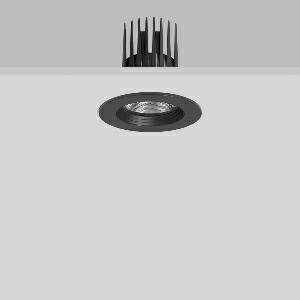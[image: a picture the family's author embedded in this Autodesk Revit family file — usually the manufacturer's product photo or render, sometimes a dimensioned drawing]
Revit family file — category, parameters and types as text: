
# Revit family: heledon_mini_e_901749_003_76_e557
name_source: partatom
category: Lighting Fixtures
units: mm (PartAtom-declared; Revit-internal decimal feet)

## family parameters
Cut with Voids When Loaded = No
Host = Face
Light Source = No
Part Type = Normal
Room Calculation Point = No
Round Connector Dimension = Use Diameter
Shared = No

## types (1)
- HELEDON mini E (1 x LED Modul 930, 3500 lm, 3000)
    Apparent Load = 29 VA
    Approval mark = CE
    CIE Flux Codes = 99 100 100 100 100
    Color Rendering = 90
    Color Temperature = 3000
    Default Elevation = 1800 mm
    Description = Series: HELEDON mini
Round recessed downlight. Housing: die-cast aluminium, powder-coated. Black plastic ring and recessed LED to prevent glare from the side. Optical assembly with reflector made of MIRO-Silver with 98% total light reflection for outstanding efficiency - can be changed without tools. Best colour rendering index Ra>90. Suitable for Recessed ceiling mounting. Installation without tools thanks to spring fastening system. Including separate LED converter with connecting cable 600 mm.High quality converter without flickering and stroboscopic effect. Through-wiring box (5 pole) available as accessory. The following accessories can be mounted without use of tools: interchangeable lenses, decorative glasses, honeycomb louvre, clear and frosted diffusers, white interchangeable plastic ring. 
Colour: deep black, matt (RAL 9005)
Diameter: 124 mm
Height: 3 mm
Cut-out diameter: 114 mm
Recess height: 170 mm
Luminaire: recess height: 120 mm
Lamp: LED
Socket: without socket
Colour temperature: 3000K
Colour rendering index (CRI): 92
System power: 29 W
Rated luminous flux: 3500 lm
Luminous efficiency: 121 lm/W
Control gear: Converter, dimmable, DALI
Protection class: II
Type of protection: IP 20
    Height = 0 mm  [stored 0 ft]
    Lamp = 1 x LED Modul 930
    Lamp Light Flux = 3500 lm
    Lamp count = 1
    Length = 124 mm  [stored 0.406824 ft]
    Lifetime = 50000 h
    Luminous efficacy = 121 lm/W
    Manufacturer = RZB
    ModVariant = No
    Model = 901749.003.76
    Mounting Place = Ceiling
    Mounting Type = Recessed
    Number of Poles = 1
    OnlyDefault = Yes
    Power Factor = 1
    Product Name = HELEDON mini E
    Product group = Recessed downlights
    ProductGroupID = 402
    Protection Class = Protection class II
    Protection Degree = IP 20
    RLX_Detail_Level = 1
    RLX_Emergency_Light_Flux = 0 lm
    RLX_Emergency_Type = 0
    RLX_Emergency_Type_DB = No
    RlxData = <blob elided: 125513 chars, md5=5a18a02f>
    Socket = socket
    Standby Power = 0 W
    System Light Flux = 3500 lm
    System Power = 29 W
    Type Comments = Product without accessories
    Type Image = 901657.003.jpg
    URL = http://relux.com
    VarID = ---
    Voltage = 230 V
    Voltage Range = 220-240 V
    Weight = 0.00 kg
    Width = 0 mm  [stored 0 ft]

note: [stored X ft] marks values corroborated as IEEE doubles in the binary element streams (Revit-internal decimal feet)

## geometry (parser evidence)
native form markers: Blend x4, Sweep x12
no freeform markers — native parametric forms only
